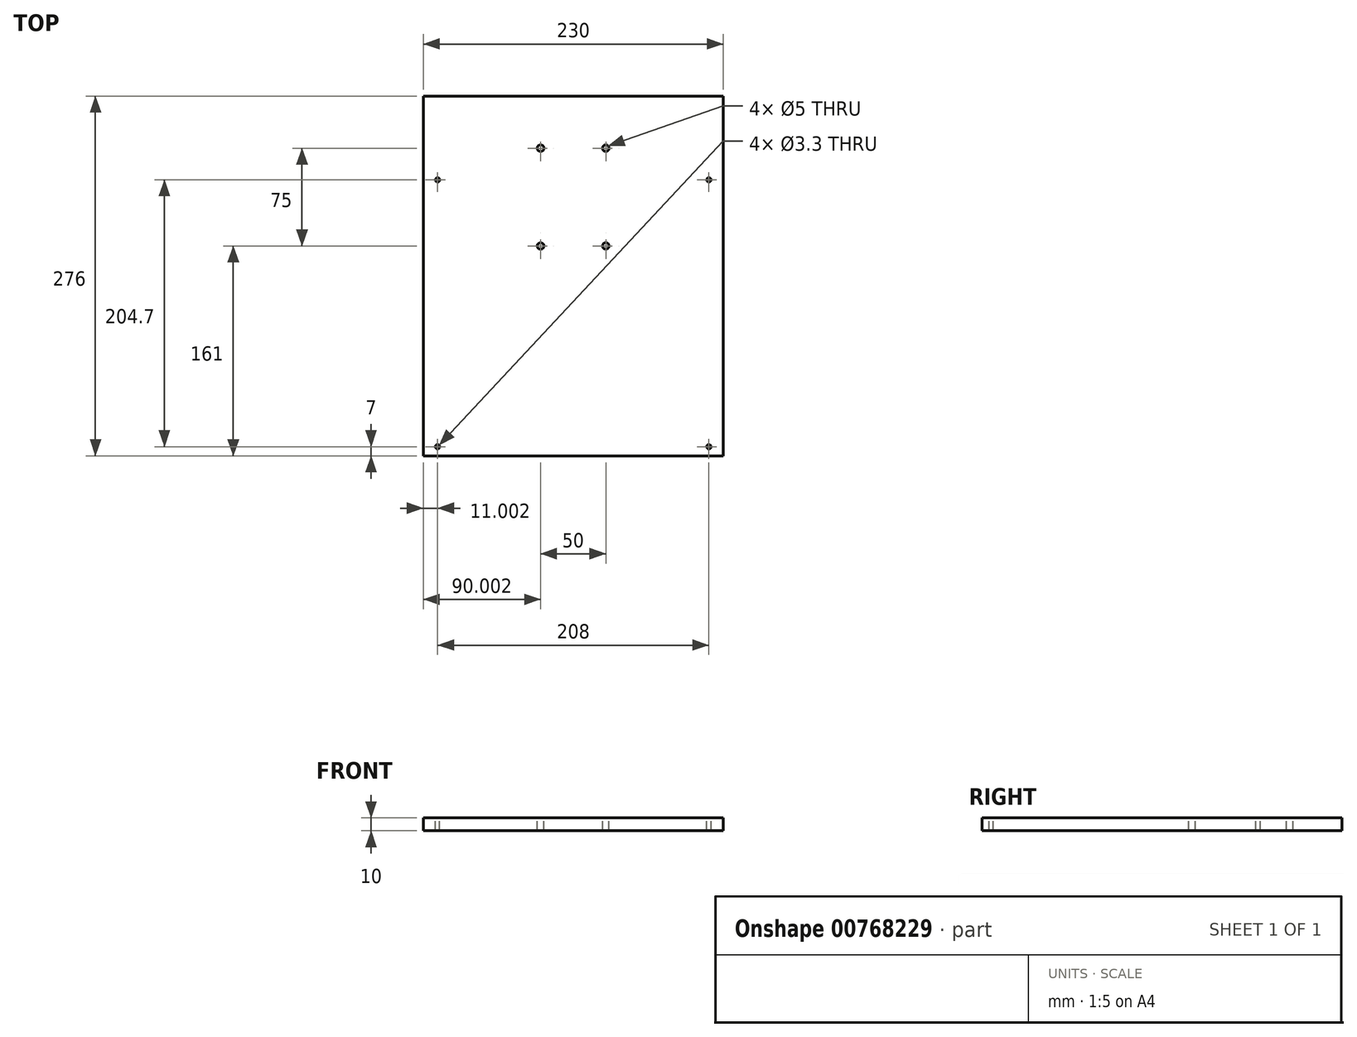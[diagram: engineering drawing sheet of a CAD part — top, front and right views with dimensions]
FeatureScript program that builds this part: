
annotation { "Feature Type Name" : "Feature", "Feature Type Description" : "" }
export const myFeature = defineFeature(function(context is Context, id is Id, definition is map)
    precondition{}
    {
        {
            var Q0;
            Q0=qCreatedBy(makeId("Top.planeOp"),FACE);
            var sketch = newSketch(context, id + "F0", { "sketchPlane" : qUnion([Q0])});
            skLineSegment(sketch, "E0.bottom", {"start": v(-44.88, 134.19) * mm, "end": v(185.12, 134.19) * mm});
            skLineSegment(sketch, "E0.top", {"start": v(-44.88, -141.81) * mm, "end": v(185.12, -141.81) * mm});
            skLineSegment(sketch, "E0.left", {"start": v(-44.88, 134.19) * mm, "end": v(-44.88, -141.81) * mm});
            skLineSegment(sketch, "E0.right", {"start": v(185.12, 134.19) * mm, "end": v(185.12, -141.81) * mm});
            skSolve(sketch);
        }
        {
            var Q0;
            Q0=qSketchRegion(id+"F0",true);
            extrude(context, id + "F1", {"entities" : qUnion([Q0]), "depth" : 10 * mm});
        }
        {
            var Q0;
            Q0=makeQuery(id+"F1.opExtrude","CAP_FACE",FACE,{"disambiguationData":[OSD([sQuery(id+"F0.wireOp",EDGE,"E0.bottom"),sQuery(id+"F0.wireOp",EDGE,"E0.top"),sQuery(id+"F0.wireOp",EDGE,"E0.left"),sQuery(id+"F0.wireOp",EDGE,"E0.right")])],"isStart":false});
            var sketch = newSketch(context, id + "F2", { "sketchPlane" : qUnion([Q0])});
            skLineSegment(sketch, "E1", {"start": v(70.12, 134.19) * mm, "end": v(70.12, -141.81) * mm, "construction": true});
            skLineSegment(sketch, "E2.bottom", {"start": v(45.12, 94.19) * mm, "end": v(95.12, 94.19) * mm, "construction": true});
            skLineSegment(sketch, "E2.top", {"start": v(45.12, 19.19) * mm, "end": v(95.12, 19.19) * mm, "construction": true});
            skLineSegment(sketch, "E2.left", {"start": v(45.12, 94.19) * mm, "end": v(45.12, 19.19) * mm, "construction": true});
            skLineSegment(sketch, "E2.right", {"start": v(95.12, 94.19) * mm, "end": v(95.12, 19.19) * mm, "construction": true});
            skCircle(sketch, "E3", {"center": v(45.12, 94.19) * mm, "radius": 2.5 * mm});
            skCircle(sketch, "E4", {"center": v(95.12, 94.19) * mm, "radius": 2.5 * mm});
            skCircle(sketch, "E5", {"center": v(45.12, 19.19) * mm, "radius": 2.5 * mm});
            skCircle(sketch, "E6", {"center": v(95.12, 19.19) * mm, "radius": 2.5 * mm});
            skLineSegment(sketch, "E7.bottom", {"start": v(-33.88, 69.89) * mm, "end": v(174.12, 69.89) * mm, "construction": true});
            skLineSegment(sketch, "E7.top", {"start": v(-33.88, -134.81) * mm, "end": v(174.12, -134.81) * mm, "construction": true});
            skLineSegment(sketch, "E7.left", {"start": v(-33.88, 69.89) * mm, "end": v(-33.88, -134.81) * mm, "construction": true});
            skLineSegment(sketch, "E7.right", {"start": v(174.12, 69.89) * mm, "end": v(174.12, -134.81) * mm, "construction": true});
            skCircle(sketch, "E8", {"center": v(-33.88, 69.89) * mm, "radius": 1.65 * mm});
            skCircle(sketch, "E9", {"center": v(174.12, 69.89) * mm, "radius": 1.65 * mm});
            skCircle(sketch, "E10", {"center": v(-33.88, -134.81) * mm, "radius": 1.65 * mm});
            skCircle(sketch, "E11", {"center": v(174.12, -134.81) * mm, "radius": 1.65 * mm});
            skSolve(sketch);
        }
        {
            var Q0;
            Q0 = qSketchRegion(id + "F2", true);
            extrude(context, id + "F3", {"entities" : qUnion([Q0]), "operationType" : NewBodyOperationType.REMOVE, "endBound" : BoundingType.THROUGH_ALL, "oppositeDirection" : true, "depth" : 25 * mm, "offsetDistance" : 25 * mm});
        }
    });
